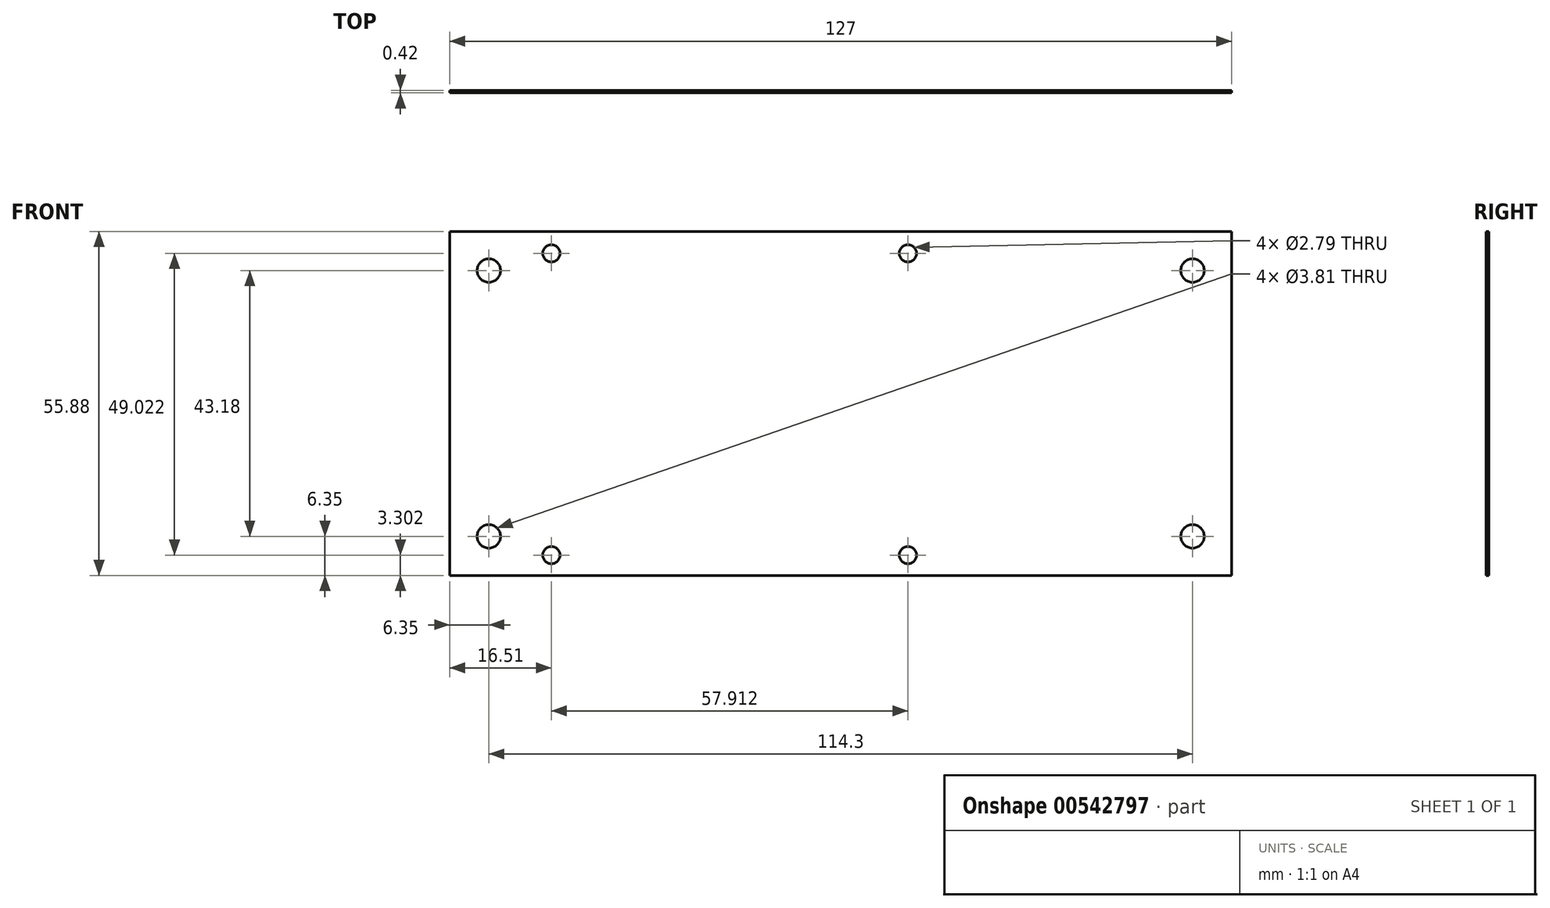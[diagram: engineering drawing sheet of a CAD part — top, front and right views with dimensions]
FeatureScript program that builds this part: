
annotation { "Feature Type Name" : "Feature", "Feature Type Description" : "" }
export const myFeature = defineFeature(function(context is Context, id is Id, definition is map)
    precondition{}
    {
        {
            var Q0;
            Q0=qCreatedBy(makeId("Front.planeOp"),FACE);
            var sketch = newSketch(context, id + "F0", { "sketchPlane" : qUnion([Q0])});
            skLineSegment(sketch, "E0.bottom", {"start": v(0, 55.88) * mm, "end": v(127, 55.88) * mm});
            skLineSegment(sketch, "E0.top", {"start": v(0, 0) * mm, "end": v(127, 0) * mm});
            skLineSegment(sketch, "E0.left", {"start": v(0, 55.88) * mm, "end": v(0, 0) * mm});
            skLineSegment(sketch, "E0.right", {"start": v(127, 55.88) * mm, "end": v(127, 0) * mm});
            skCircle(sketch, "E1", {"center": v(16.51, 3.3) * mm, "radius": 1.4 * mm});
            skCircle(sketch, "E2", {"center": v(16.51, 52.32) * mm, "radius": 1.4 * mm});
            skCircle(sketch, "E3", {"center": v(74.42, 52.32) * mm, "radius": 1.4 * mm});
            skCircle(sketch, "E4", {"center": v(74.42, 3.3) * mm, "radius": 1.4 * mm});
            skCircle(sketch, "E5", {"center": v(6.35, 49.53) * mm, "radius": 1.9 * mm});
            skCircle(sketch, "E6", {"center": v(6.35, 6.35) * mm, "radius": 1.9 * mm});
            skCircle(sketch, "E7", {"center": v(120.65, 49.53) * mm, "radius": 1.9 * mm});
            skCircle(sketch, "E8", {"center": v(120.65, 6.35) * mm, "radius": 1.9 * mm});
            skSolve(sketch);
        }
        {
            var Q0;
            Q0=makeQuery(id+"F0.imprint","IMPRINT",FACE,{"disambiguationData":[TD([[makeQuery(id+"F0.imprint","IMPRINT",EDGE,{"derivedFrom":sQuery(id+"F0.wireOp",EDGE,"E0.bottom")}),-1.0]])]});
            extrude(context, id + "F1", {"entities" : qUnion([Q0]), "depth" : 0.42 * mm, "offsetDistance" : 25.4 * mm});
        }
    });
